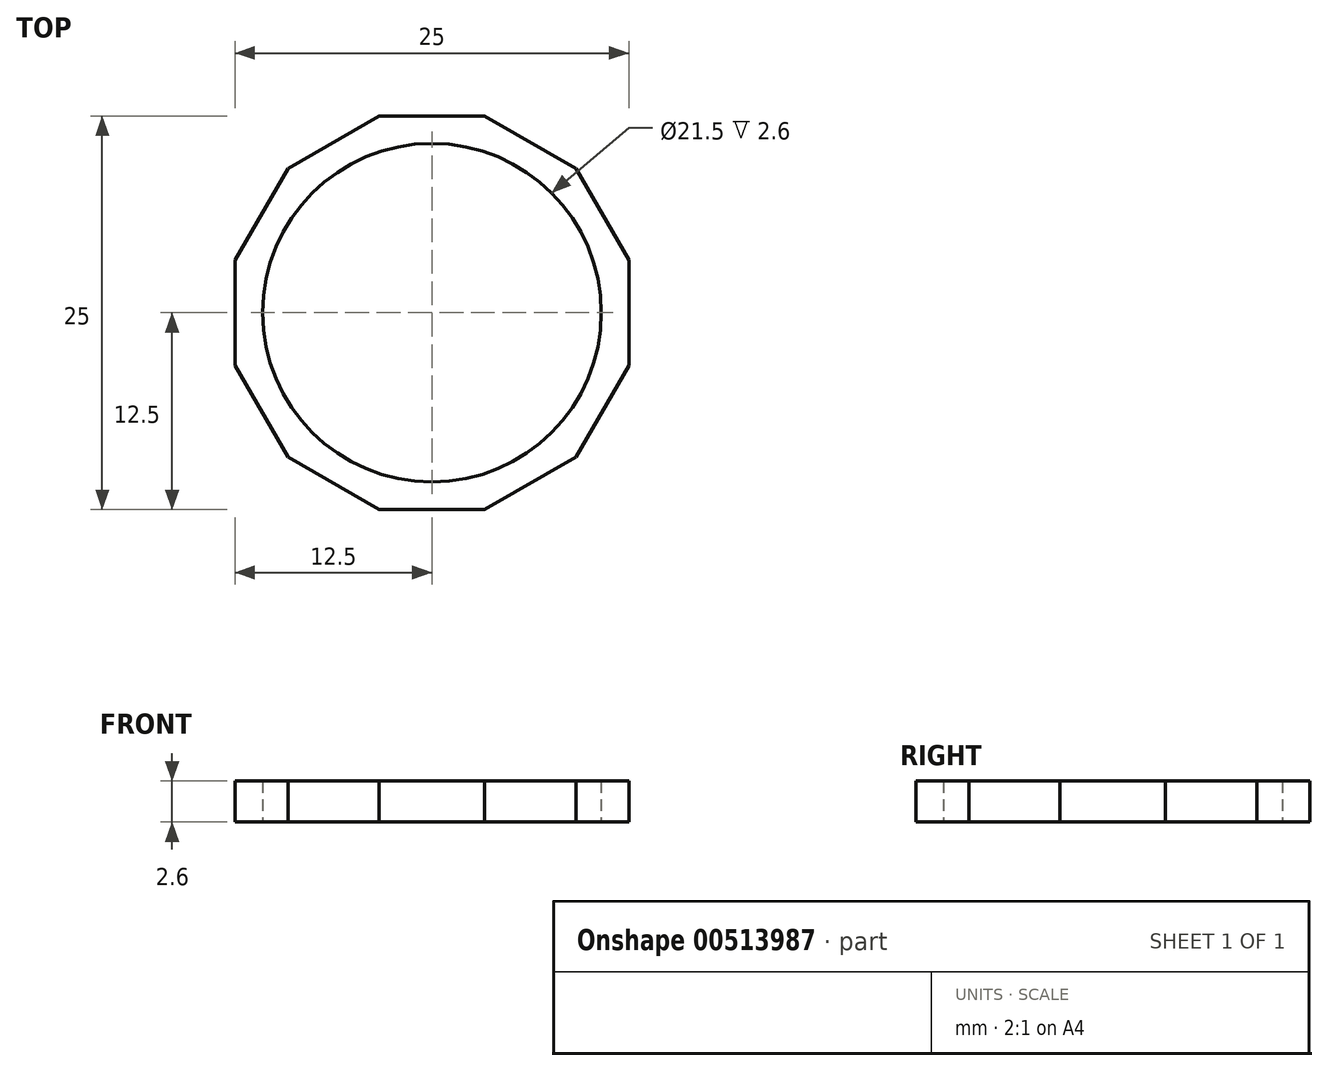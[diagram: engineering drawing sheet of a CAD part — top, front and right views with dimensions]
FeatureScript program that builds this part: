
annotation { "Feature Type Name" : "Feature", "Feature Type Description" : "" }
export const myFeature = defineFeature(function(context is Context, id is Id, definition is map)
    precondition{}
    {
        {
            var Q0;
            Q0=qCreatedBy(makeId("Top.planeOp"),FACE);
            var sketch = newSketch(context, id + "F0", { "sketchPlane" : qUnion([Q0])});
            skCircle(sketch, "E0", {"center": v(0, 0) * mm, "radius": 10.75 * mm});
            skCircle(sketch, "E1.cCircle", {"center": v(0, 0) * mm, "radius": 12.5 * mm, "construction": true});
            skLineSegment(sketch, "E1.0", {"start": v(-3.35, 12.5) * mm, "end": v(3.35, 12.5) * mm});
            skLineSegment(sketch, "E1.1", {"start": v(3.35, 12.5) * mm, "end": v(9.15, 9.15) * mm});
            skLineSegment(sketch, "E1.2", {"start": v(9.15, 9.15) * mm, "end": v(12.5, 3.35) * mm});
            skLineSegment(sketch, "E1.3", {"start": v(12.5, 3.35) * mm, "end": v(12.5, -3.35) * mm});
            skLineSegment(sketch, "E1.4", {"start": v(12.5, -3.35) * mm, "end": v(9.15, -9.15) * mm});
            skLineSegment(sketch, "E1.5", {"start": v(9.15, -9.15) * mm, "end": v(3.35, -12.5) * mm});
            skLineSegment(sketch, "E1.6", {"start": v(3.35, -12.5) * mm, "end": v(-3.35, -12.5) * mm});
            skLineSegment(sketch, "E1.7", {"start": v(-3.35, -12.5) * mm, "end": v(-9.15, -9.15) * mm});
            skLineSegment(sketch, "E1.8", {"start": v(-9.15, -9.15) * mm, "end": v(-12.5, -3.35) * mm});
            skLineSegment(sketch, "E1.9", {"start": v(-12.5, -3.35) * mm, "end": v(-12.5, 3.35) * mm});
            skLineSegment(sketch, "E1.10", {"start": v(-12.5, 3.35) * mm, "end": v(-9.15, 9.15) * mm});
            skLineSegment(sketch, "E1.11", {"start": v(-9.15, 9.15) * mm, "end": v(-3.35, 12.5) * mm});
            skPoint(sketch, "E1.0.midPoint", {"position": v(0, 12.5) * mm});
            skSolve(sketch);
        }
        {
            var Q0;
            Q0=makeQuery(id+"F0.imprint","IMPRINT",FACE,{"disambiguationData":[TD([[makeQuery(id+"F0.imprint","IMPRINT",EDGE,{"derivedFrom":sQuery(id+"F0.wireOp",EDGE,"E0")}),-1.0]])]});
            extrude(context, id + "F1", {"entities" : qUnion([Q0]), "depth" : 2.6 * mm});
        }
    });
